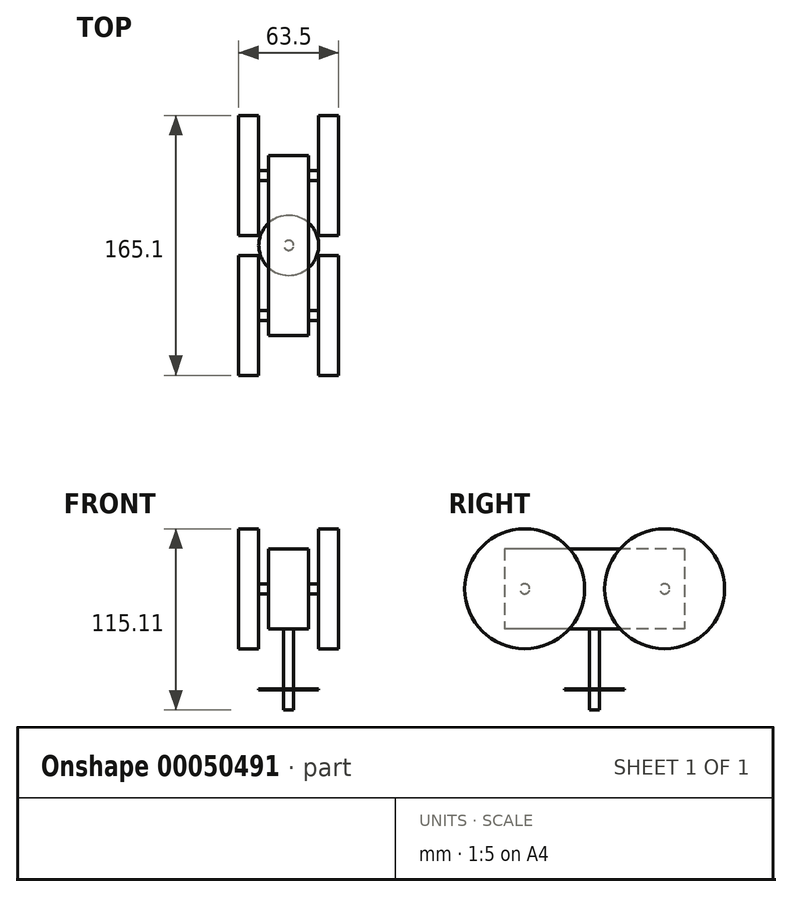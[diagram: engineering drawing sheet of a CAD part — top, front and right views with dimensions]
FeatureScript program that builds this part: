
annotation { "Feature Type Name" : "Feature", "Feature Type Description" : "" }
export const myFeature = defineFeature(function(context is Context, id is Id, definition is map)
    precondition{}
    {
        {
            var Q0;
            Q0=qCreatedBy(makeId("Right.planeOp"),FACE);
            var sketch = newSketch(context, id + "F0", { "sketchPlane" : qUnion([Q0])});
            skLineSegment(sketch, "E0.rect.bottom", {"start": v(57.15, 25.4) * mm, "end": v(-57.15, 25.4) * mm});
            skLineSegment(sketch, "E0.rect.top", {"start": v(57.15, -25.4) * mm, "end": v(-57.15, -25.4) * mm});
            skLineSegment(sketch, "E0.rect.left", {"start": v(57.15, 25.4) * mm, "end": v(57.15, -25.4) * mm});
            skLineSegment(sketch, "E0.rect.right", {"start": v(-57.15, 25.4) * mm, "end": v(-57.15, -25.4) * mm});
            skPoint(sketch, "E0.rect.middle", {"position": v(0, 0) * mm});
            skSolve(sketch);
        }
        {
            var Q0;
            Q0 = qSketchRegion(id + "F0", true);
            extrude(context, id + "F1", {"entities" : qUnion([Q0]), "endBound" : BoundingType.SYMMETRIC, "depth" : 25.4 * mm});
        }
        {
            var Q0;
            Q0=makeQuery(id+"F1.opExtrude","SWEPT_FACE",FACE,{"disambiguationData":[OSD([sQuery(id+"F0.wireOp",EDGE,"E0.rect.top")])]});
            var sketch = newSketch(context, id + "F2", { "sketchPlane" : qUnion([Q0])});
            skCircle(sketch, "E1", {"center": v(0, 0) * mm, "radius": 3.18 * mm});
            skSolve(sketch);
        }
        {
            var Q0;
            Q0 = qSketchRegion(id + "F2", true);
            extrude(context, id + "F3", {"entities" : qUnion([Q0]), "operationType" : NewBodyOperationType.ADD, "depth" : 38.1 * mm});
        }
        {
            var Q0;
            Q0=makeQuery(id+"F1.opExtrude","CAP_FACE",FACE,{"disambiguationData":[OSD([sQuery(id+"F0.wireOp",EDGE,"E0.rect.bottom"),sQuery(id+"F0.wireOp",EDGE,"E0.rect.top"),sQuery(id+"F0.wireOp",EDGE,"E0.rect.left"),sQuery(id+"F0.wireOp",EDGE,"E0.rect.right")])],"isStart":false});
            var sketch = newSketch(context, id + "F4", { "sketchPlane" : qUnion([Q0])});
            skCircle(sketch, "E2", {"center": v(-44.45, 0) * mm, "radius": 38.1 * mm, "construction": true});
            skCircle(sketch, "E3", {"center": v(44.45, 0) * mm, "radius": 38.1 * mm, "construction": true});
            skLineSegment(sketch, "E4", {"start": v(-44.45, 0) * mm, "end": v(0, 0) * mm, "construction": true});
            skLineSegment(sketch, "E5", {"start": v(0, 0) * mm, "end": v(44.45, 0) * mm, "construction": true});
            skLineSegment(sketch, "E6", {"start": v(-57.15, 0) * mm, "end": v(-44.45, 0) * mm, "construction": true});
            skLineSegment(sketch, "E7", {"start": v(44.45, 0) * mm, "end": v(57.15, 0) * mm, "construction": true});
            skCircle(sketch, "E8", {"center": v(-44.45, 0) * mm, "radius": 3.18 * mm});
            skCircle(sketch, "E9", {"center": v(44.45, 0) * mm, "radius": 3.18 * mm});
            skSolve(sketch);
        }
        {
            var Q0;
            Q0 = qSketchRegion(id + "F4", true);
            extrude(context, id + "F5", {"entities" : qUnion([Q0]), "operationType" : NewBodyOperationType.ADD, "depth" : 6.35 * mm});
        }
        {
            var Q0;
            Q0=makeQuery(id+"F5.opExtrude","CAP_FACE",FACE,{"disambiguationData":[OSD([sQuery(id+"F4.wireOp",EDGE,"E8")])],"isStart":false});
            var sketch = newSketch(context, id + "F6", { "sketchPlane" : qUnion([Q0])});
            skCircle(sketch, "E10", {"center": v(-44.45, 0) * mm, "radius": 38.1 * mm});
            skCircle(sketch, "E11", {"center": v(44.45, 0) * mm, "radius": 38.1 * mm});
            skLineSegment(sketch, "E12", {"start": v(-44.45, 0) * mm, "end": v(0, 0) * mm, "construction": true});
            skLineSegment(sketch, "E13", {"start": v(0, 0) * mm, "end": v(44.45, 0) * mm, "construction": true});
            skSolve(sketch);
        }
        {
            var Q0;
            Q0 = qSketchRegion(id + "F6", true);
            extrude(context, id + "F7", {"entities" : qUnion([Q0]), "operationType" : NewBodyOperationType.ADD, "depth" : 12.7 * mm});
        }
        {
            var Q0;
            Q0=makeQuery(id+"F1.opExtrude","SWEPT_BODY",BODY,{"disambiguationData":[OSD([sQuery(id+"F0.wireOp",EDGE,"E0.rect.bottom"),sQuery(id+"F0.wireOp",EDGE,"E0.rect.top"),sQuery(id+"F0.wireOp",EDGE,"E0.rect.left"),sQuery(id+"F0.wireOp",EDGE,"E0.rect.right")])]});
            var Q1;
            Q1=qCreatedBy(makeId("Right.planeOp"),FACE);
            mirror(context, id + "F8", {"operationType" : NewBodyOperationType.ADD, "entities" : qUnion([Q0]), "mirrorPlane" : qUnion([Q1])});
        }
        {
            var Q0;
            Q0=makeQuery(id+"F3.opExtrude","CAP_FACE",FACE,{"disambiguationData":[OSD([sQuery(id+"F2.wireOp",EDGE,"E1")])],"isStart":false});
            var sketch = newSketch(context, id + "F9", { "sketchPlane" : qUnion([Q0])});
            skCircle(sketch, "E14", {"center": v(0, 0) * mm, "radius": 19.05 * mm});
            skSolve(sketch);
        }
        {
            var Q0;
            Q0 = qSketchRegion(id + "F9", true);
            extrude(context, id + "F10", {"entities" : qUnion([Q0]), "operationType" : NewBodyOperationType.ADD, "depth" : 0.81 * mm});
        }
        {
            var Q0;
            Q0=makeQuery(id+"F10.opExtrude","CAP_FACE",FACE,{"disambiguationData":[OSD([sQuery(id+"F9.wireOp",EDGE,"E14")])],"isStart":false});
            var sketch = newSketch(context, id + "F11", { "sketchPlane" : qUnion([Q0])});
            skCircle(sketch, "E15", {"center": v(0, 0) * mm, "radius": 3.18 * mm});
            skSolve(sketch);
        }
        {
            var Q0;
            Q0 = qSketchRegion(id + "F11", true);
            extrude(context, id + "F12", {"entities" : qUnion([Q0]), "operationType" : NewBodyOperationType.ADD, "depth" : 12.7 * mm});
        }
    });
